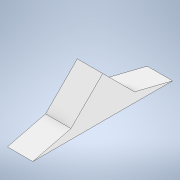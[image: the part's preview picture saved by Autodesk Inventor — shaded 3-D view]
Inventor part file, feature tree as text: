
AUTODESK INVENTOR PART (.ipt)
format: ipt  version: 2021.1 (Build 251245000, 245)  size: 107,520 bytes
history: native  units: in
note: dims shown in document units (in); Inventor stores cm internally (conversion verified against a paired STEP export)
features: extrude x1, mirror x1, sketch x1
ambient origin geometry x8: Origin, YZ Plane, XZ Plane, XY Plane, X Axis, Y Axis, Z Axis, Center Point
bodies: Solid1 (feature_tree)
feature tree (3):
  extrude  "Extrusion1"  TaperAngle=45.0deg  [1 undecoded]
  mirror  "Mirror1"
  sketch  "Sketch1"  dims[d3=96.0in d4=0.0in d9=45.0deg d10=120.0in]
note: 1 required parameter value undecoded (feature->parameter linkage not recoverable at this tier; creation-order binding heuristic only, values carry confidence <= 0.55)
